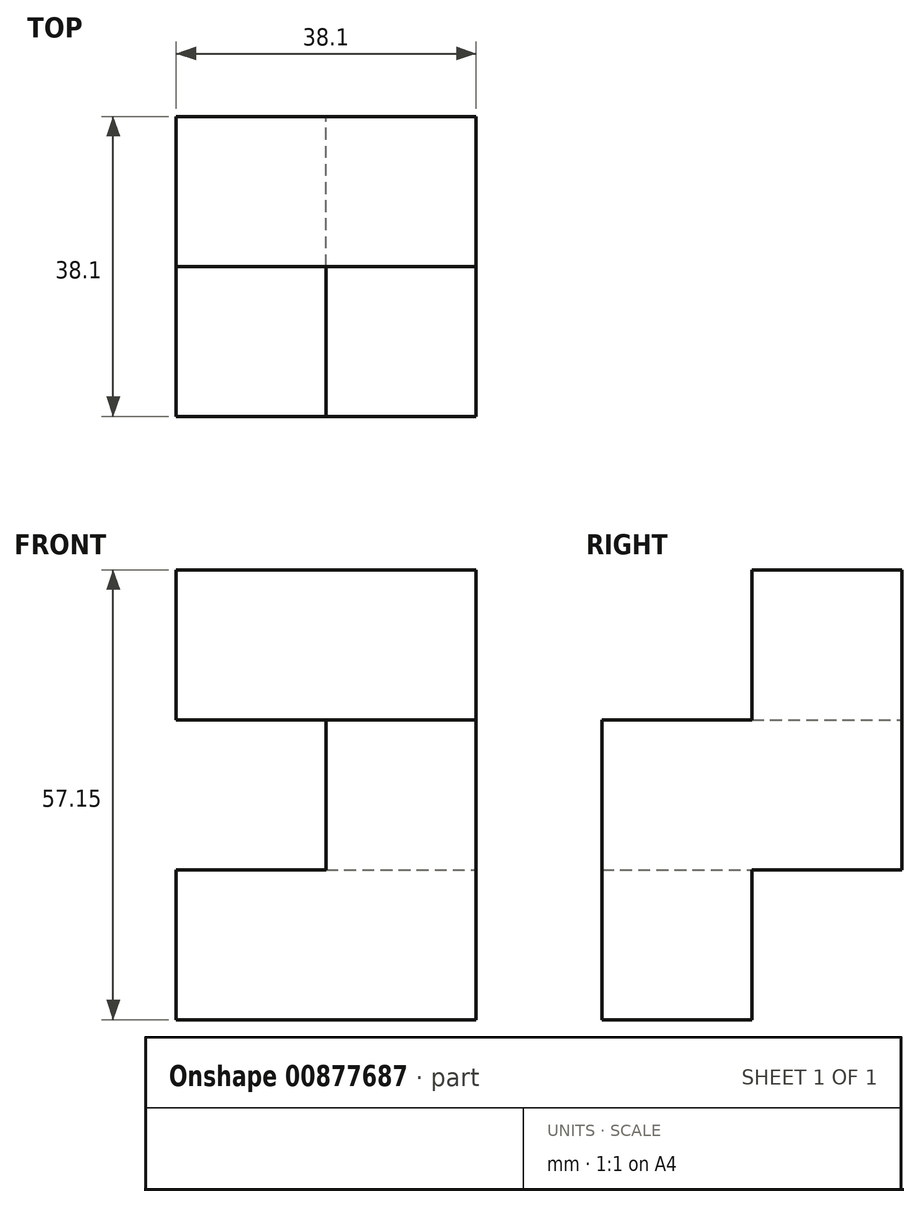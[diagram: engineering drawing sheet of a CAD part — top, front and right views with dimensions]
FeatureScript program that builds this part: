
annotation { "Feature Type Name" : "Feature", "Feature Type Description" : "" }
export const myFeature = defineFeature(function(context is Context, id is Id, definition is map)
    precondition{}
    {
        {
            var Q0;
            Q0=qCreatedBy(makeId("Top.planeOp"),FACE);
            var sketch = newSketch(context, id + "F0", { "sketchPlane" : qUnion([Q0])});
            skLineSegment(sketch, "E0.bottom", {"start": v(19.05, -38.1) * mm, "end": v(57.15, -38.1) * mm});
            skLineSegment(sketch, "E0.top", {"start": v(19.05, -57.15) * mm, "end": v(57.15, -57.15) * mm});
            skLineSegment(sketch, "E0.left", {"start": v(19.05, -38.1) * mm, "end": v(19.05, -57.15) * mm});
            skLineSegment(sketch, "E0.right", {"start": v(57.15, -38.1) * mm, "end": v(57.15, -57.15) * mm});
            skSolve(sketch);
        }
        {
            var Q0;
            Q0=qSketchRegion(id+"F0",true);
            extrude(context, id + "F1", {"entities" : qUnion([Q0]), "depth" : 19.05 * mm});
        }
        {
            var Q0;
            Q0=makeQuery(id+"F1.opExtrude","CAP_FACE",FACE,{"disambiguationData":[OSD([sQuery(id+"F0.wireOp",EDGE,"E0.bottom"),sQuery(id+"F0.wireOp",EDGE,"E0.top"),sQuery(id+"F0.wireOp",EDGE,"E0.left"),sQuery(id+"F0.wireOp",EDGE,"E0.right")])],"isStart":false});
            var sketch = newSketch(context, id + "F2", { "sketchPlane" : qUnion([Q0])});
            skLineSegment(sketch, "E1.bottom", {"start": v(57.15, -57.15) * mm, "end": v(38.1, -57.15) * mm});
            skLineSegment(sketch, "E2", {"start": v(38.1, -57.15) * mm, "end": v(38.1, -19.05) * mm});
            skLineSegment(sketch, "E3", {"start": v(38.1, -19.05) * mm, "end": v(57.15, -19.05) * mm});
            skLineSegment(sketch, "E4", {"start": v(57.15, -6.35) * mm, "end": v(57.15, -57.15) * mm});
            skSolve(sketch);
        }
        {
            var Q0;
            Q0=qSketchRegion(id+"F2",true);
            extrude(context, id + "F3", {"entities" : qUnion([Q0]), "operationType" : NewBodyOperationType.ADD, "depth" : 19.05 * mm});
        }
        {
            var Q0;
            Q0=qSketchRegion(id+"F2",true);
            extrude(context, id + "F4", {"entities" : qUnion([Q0]), "operationType" : NewBodyOperationType.ADD, "depth" : 19.05 * mm});
        }
        {
            var Q0;
            Q0=makeQuery(id+"F3.opExtrude","CAP_FACE",FACE,{"disambiguationData":[OSD([sQuery(id+"F2.wireOp",EDGE,"E1.bottom"),sQuery(id+"F2.wireOp",EDGE,"E2"),sQuery(id+"F2.wireOp",EDGE,"E3"),sQuery(id+"F2.wireOp",EDGE,"E4")])],"isStart":false});
            var sketch = newSketch(context, id + "F5", { "sketchPlane" : qUnion([Q0])});
            skLineSegment(sketch, "E5.bottom", {"start": v(57.15, -38.1) * mm, "end": v(19.05, -38.1) * mm});
            skLineSegment(sketch, "E5.top", {"start": v(57.15, -19.05) * mm, "end": v(19.05, -19.05) * mm});
            skLineSegment(sketch, "E5.left", {"start": v(57.15, -38.1) * mm, "end": v(57.15, -19.05) * mm});
            skLineSegment(sketch, "E5.right", {"start": v(19.05, -38.1) * mm, "end": v(19.05, -19.05) * mm});
            skSolve(sketch);
        }
        {
            var Q0;
            Q0=qSketchRegion(id+"F5",true);
            extrude(context, id + "F6", {"entities" : qUnion([Q0]), "operationType" : NewBodyOperationType.ADD, "depth" : 19.05 * mm});
        }
    });
